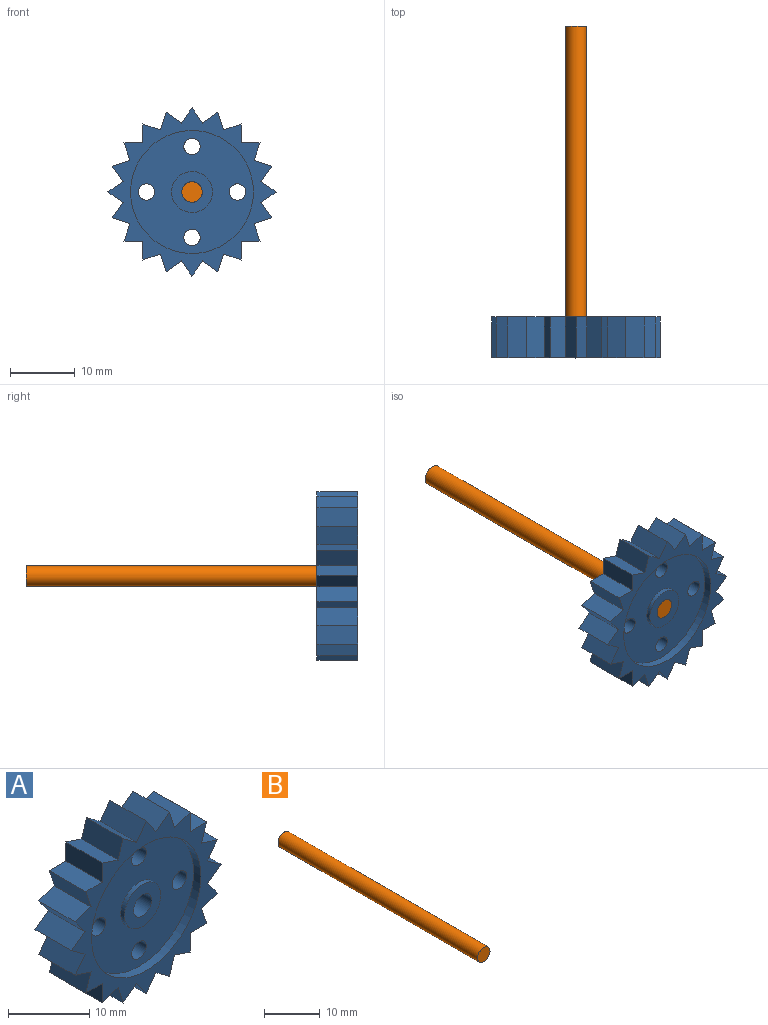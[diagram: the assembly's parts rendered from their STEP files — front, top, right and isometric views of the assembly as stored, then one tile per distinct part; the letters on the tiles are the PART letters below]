
ASSEMBLY  parts=2 mates=1
PART A: 55 faces, bbox 26.1x6.4x26.1 mm
  f0: plane 26.06x26.06mm, normal (0,-1,0), area 155mm2, adj f2,f3,f4,f5,f6,f7,f8,f9
  f1: plane 26.06x26.06mm, normal (0,1,0), area 155mm2, adj f2,f3,f4,f5,f6,f7,f8,f9
  f2: plane 6.35x2.37mm, normal (0.81,0,0.58), area 18.5mm2, adj f0,f1,f3,f5
  f3: plane 6.35x2.37mm, normal (-0.81,0,0.58), area 18.5mm2, adj f0,f1,f2,f40
  f4: plane 6.35x2.77mm, normal (0.95,0,0.3), area 18.5mm2, adj f0,f1,f5,f7
  f5: plane 6.35x2.34mm, normal (-0.59,0,0.8), area 18.5mm2, adj f0,f1,f2,f4
  f6: plane 6.35x2.91mm, normal (1,0,-0.01), area 18.5mm2, adj f0,f1,f7,f9
  f7: plane 6.35x2.76mm, normal (-0.32,0,0.95), area 18.5mm2, adj f0,f1,f4,f6
  f8: plane 6.35x2.76mm, normal (0.95,0,-0.32), area 18.5mm2, adj f0,f1,f9,f11
  f9: plane 6.35x2.91mm, normal (-0.01,0,1), area 18.5mm2, adj f0,f1,f6,f8
  f10: plane 6.35x2.34mm, normal (0.8,0,-0.59), area 18.5mm2, adj f0,f1,f11,f13
  f11: plane 6.35x2.77mm, normal (0.3,0,0.95), area 18.5mm2, adj f0,f1,f8,f10
  f12: plane 6.35x2.37mm, normal (0.58,0,-0.81), area 18.5mm2, adj f0,f1,f13,f15
  f13: plane 6.35x2.37mm, normal (0.58,0,0.81), area 18.5mm2, adj f0,f1,f10,f12
  f14: plane 6.35x2.77mm, normal (0.3,0,-0.95), area 18.5mm2, adj f0,f1,f15,f17
  f15: plane 6.35x2.34mm, normal (0.8,0,0.59), area 18.5mm2, adj f0,f1,f12,f14
  f16: plane 6.35x2.91mm, normal (-0.01,0,-1), area 18.5mm2, adj f0,f1,f17,f19
  f17: plane 6.35x2.76mm, normal (0.95,0,0.32), area 18.5mm2, adj f0,f1,f14,f16
  f18: plane 6.35x2.76mm, normal (-0.32,0,-0.95), area 18.5mm2, adj f0,f1,f19,f21
  f19: plane 6.35x2.91mm, normal (1,0,0.01), area 18.5mm2, adj f0,f1,f16,f18
  f20: plane 6.35x2.34mm, normal (-0.59,0,-0.8), area 18.5mm2, adj f0,f1,f21,f23
  f21: plane 6.35x2.77mm, normal (0.95,0,-0.3), area 18.5mm2, adj f0,f1,f18,f20
  f22: plane 6.35x2.37mm, normal (-0.81,0,-0.58), area 18.5mm2, adj f0,f1,f23,f25
  f23: plane 6.35x2.37mm, normal (0.81,0,-0.58), area 18.5mm2, adj f0,f1,f20,f22
  f24: plane 6.35x2.77mm, normal (-0.95,0,-0.3), area 18.5mm2, adj f0,f1,f25,f27
  f25: plane 6.35x2.34mm, normal (0.59,0,-0.8), area 18.5mm2, adj f0,f1,f22,f24
  f26: plane 6.35x2.91mm, normal (-1,0,0.01), area 18.5mm2, adj f0,f1,f27,f29
  f27: plane 6.35x2.76mm, normal (0.32,0,-0.95), area 18.5mm2, adj f0,f1,f24,f26
  f28: plane 6.35x2.76mm, normal (-0.95,0,0.32), area 18.5mm2, adj f0,f1,f29,f31
  f29: plane 6.35x2.91mm, normal (0.01,0,-1), area 18.5mm2, adj f0,f1,f26,f28
  f30: plane 6.35x2.34mm, normal (-0.8,0,0.59), area 18.5mm2, adj f0,f1,f31,f33
  f31: plane 6.35x2.77mm, normal (-0.3,0,-0.95), area 18.5mm2, adj f0,f1,f28,f30
  f32: plane 6.35x2.37mm, normal (-0.58,0,0.81), area 18.5mm2, adj f0,f1,f33,f35
  f33: plane 6.35x2.37mm, normal (-0.58,0,-0.81), area 18.5mm2, adj f0,f1,f30,f32
  f34: plane 6.35x2.77mm, normal (-0.3,0,0.95), area 18.5mm2, adj f0,f1,f35,f37
  f35: plane 6.35x2.34mm, normal (-0.8,0,-0.59), area 18.5mm2, adj f0,f1,f32,f34
  f36: plane 6.35x2.91mm, normal (0.01,0,1), area 18.5mm2, adj f0,f1,f37,f39
  f37: plane 6.35x2.76mm, normal (-0.95,0,-0.32), area 18.5mm2, adj f0,f1,f34,f36
  f38: plane 6.35x2.76mm, normal (0.32,0,0.95), area 18.5mm2, adj f0,f1,f39,f41
  f39: plane 6.35x2.91mm, normal (-1,0,-0.01), area 18.5mm2, adj f0,f1,f36,f38
  f40: plane 6.35x2.34mm, normal (0.59,0,0.8), area 18.5mm2, adj f0,f1,f3,f41
  f41: plane 6.35x2.77mm, normal (-0.95,0,0.3), area 18.5mm2, adj f0,f1,f38,f40
  f42: cylinder r=9.53mm len=19.05mm, axis (0,1,0), area 76mm2, adj f1,f43
  f43: plane 19.05x19.05mm, normal (0,1,0), area 233.1mm2, adj f42,f46,f47,f48,f49,f50
  f44: cylinder r=9.53mm len=19.05mm, axis (0,-1,0), area 76mm2, adj f0,f45
  f45: plane 19.05x19.05mm, normal (0,-1,0), area 233.1mm2, adj f44,f46,f47,f48,f49,f52
  f46: cylinder r=1.27mm len=3.81mm, axis (0,1,0), area 30.4mm2, adj f43,f45
  f47: cylinder r=1.27mm len=3.81mm, axis (0,1,0), area 30.4mm2, adj f43,f45
  f48: cylinder r=1.27mm len=3.81mm, axis (0,1,0), area 30.4mm2, adj f43,f45
  f49: cylinder r=1.27mm len=3.81mm, axis (0,1,0), area 30.4mm2, adj f43,f45
  f50: cylinder r=3.17mm len=6.35mm, axis (0,-1,0), area 12.7mm2, adj f43,f51
  f51: plane 6.35x6.35mm, normal (0,1,0), area 23.8mm2, adj f50,f54
  f52: cylinder r=3.17mm len=6.35mm, axis (0,1,0), area 12.7mm2, adj f45,f53
  f53: plane 6.35x6.35mm, normal (0,-1,0), area 23.8mm2, adj f52,f54
  f54: cylinder r=1.59mm len=5.08mm, axis (0,1,0), area 50.7mm2, adj f51,f53
PART B: 3 faces, bbox 3.2x50.8x3.2 mm
  f0: cylinder r=1.59mm len=50.8mm, axis (0,1,0), area 506.7mm2, adj f1,f2
  f1: plane 3.18x3.18mm, normal (0,-1,0), area 7.9mm2, adj f0
  f2: plane 3.18x3.18mm, normal (0,1,0), area 7.9mm2, adj f0
PLACE A t=(0,2.54,0)mm
PLACE B t=(0,25.4,0)mm
MATE fastened A.f42 <-> B.f0  axis (0,-1,0) through (0,0,0)mm
